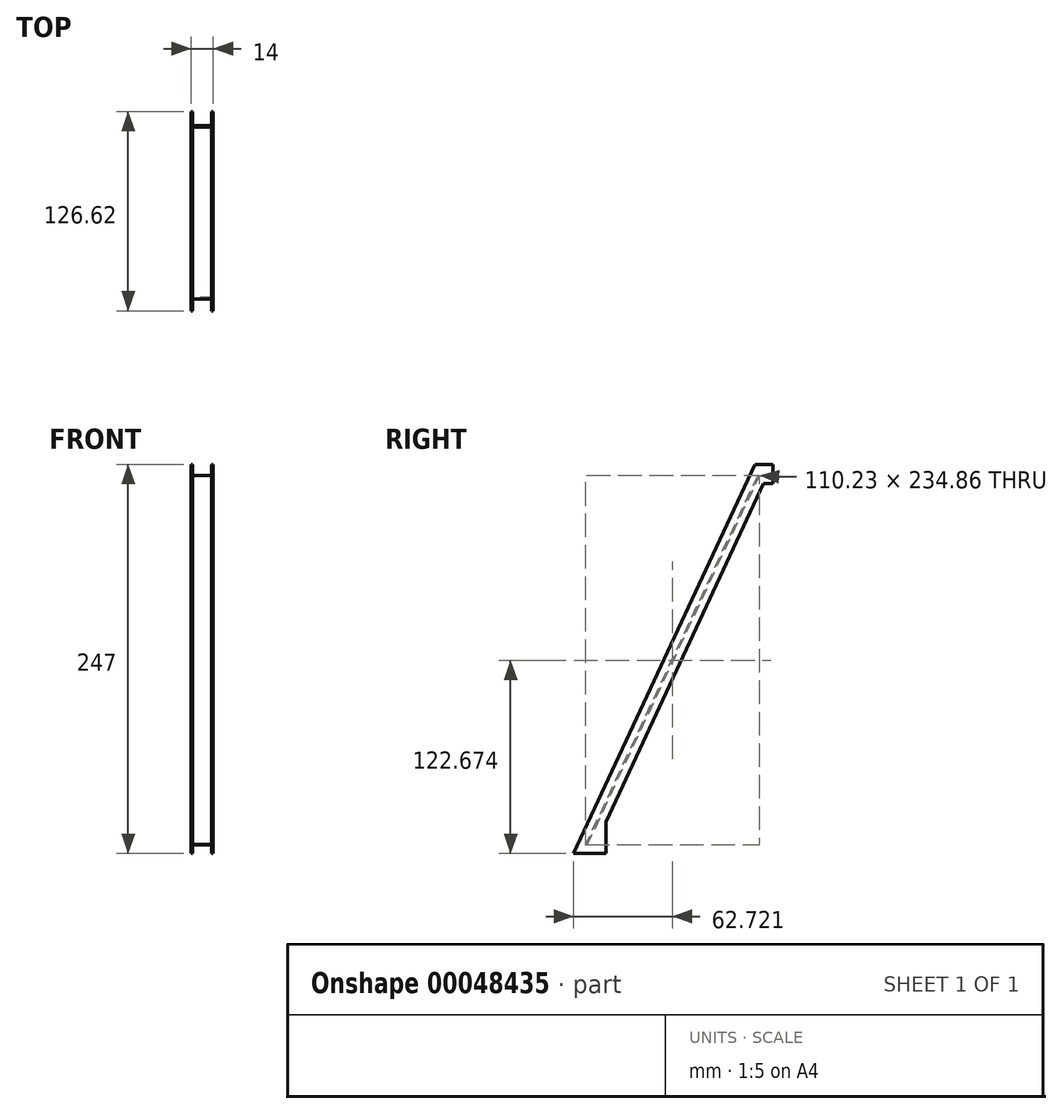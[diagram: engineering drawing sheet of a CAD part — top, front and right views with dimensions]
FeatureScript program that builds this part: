
annotation { "Feature Type Name" : "Feature", "Feature Type Description" : "" }
export const myFeature = defineFeature(function(context is Context, id is Id, definition is map)
    precondition{}
    {
        {
            var Q0;
            Q0=qCreatedBy(makeId("Right.planeOp"),FACE);
            cPlane(context, id + "F0", {"entities" : qUnion([Q0]), "cplaneType" : CPlaneType.OFFSET, "offset" : 7 * mm, "oppositeDirection" : true, "width" : 150 * mm, "height" : 150 * mm});
        }
        {
            var Q0;
            Q0=qCreatedBy(id+"F0.planeOp",FACE);
            var sketch = newSketch(context, id + "F1", { "sketchPlane" : qUnion([Q0])});
            skLineSegment(sketch, "E0", {"start": v(0, 0) * mm, "end": v(115.18, 247) * mm});
            skLineSegment(sketch, "E1", {"start": v(115.18, 247) * mm, "end": v(126.62, 247) * mm});
            skLineSegment(sketch, "E2", {"start": v(126.62, 247) * mm, "end": v(126.62, 235) * mm});
            skLineSegment(sketch, "E3", {"start": v(126.62, 235) * mm, "end": v(120.62, 235) * mm});
            skLineSegment(sketch, "E4", {"start": v(120.62, 235) * mm, "end": v(20.36, 20) * mm});
            skLineSegment(sketch, "E5", {"start": v(20.36, 20) * mm, "end": v(20.36, 0) * mm});
            skLineSegment(sketch, "E6", {"start": v(20.36, 0) * mm, "end": v(0, 0) * mm});
            skSolve(sketch);
        }
        {
            var Q0;
            Q0=makeQuery(id+"F1.imprint","IMPRINT",FACE,{"disambiguationData":[TD([[makeQuery(id+"F1.imprint","IMPRINT",EDGE,{"derivedFrom":sQuery(id+"F1.wireOp",EDGE,"E0")}),-1.0]])]});
            extrude(context, id + "F2", {"entities" : qUnion([Q0]), "depth" : 1 * mm});
        }
        {
            var Q0;
            Q0=makeQuery(id+"F2.opExtrude","SWEPT_BODY",BODY,{"disambiguationData":[OSD([sQuery(id+"F1.wireOp",EDGE,"E0"),sQuery(id+"F1.wireOp",EDGE,"E1"),sQuery(id+"F1.wireOp",EDGE,"E2"),sQuery(id+"F1.wireOp",EDGE,"E3"),sQuery(id+"F1.wireOp",EDGE,"E4"),sQuery(id+"F1.wireOp",EDGE,"E5"),sQuery(id+"F1.wireOp",EDGE,"E6")])]});
            var Q1;
            Q1=qCreatedBy(makeId("Right.planeOp"),FACE);
            mirror(context, id + "F3", {"entities" : qUnion([Q0]), "mirrorPlane" : qUnion([Q1])});
        }
        {
            var Q0;
            Q0=qCreatedBy(makeId("Right.planeOp"),FACE);
            var sketch = newSketch(context, id + "F4", { "sketchPlane" : qUnion([Q0])});
            skLineSegment(sketch, "E7", {"start": v(115.18, 247) * mm, "end": v(120.62, 235) * mm, "construction": true});
            skLineSegment(sketch, "E8", {"start": v(117.9, 241) * mm, "end": v(5.52, 0) * mm, "construction": true});
            skLineSegment(sketch, "E9", {"start": v(116.93, 240.1) * mm, "end": v(7.6, 5.67) * mm});
            skLineSegment(sketch, "E10", {"start": v(7.6, 5.67) * mm, "end": v(8.51, 5.24) * mm});
            skLineSegment(sketch, "E11", {"start": v(8.51, 5.24) * mm, "end": v(117.83, 239.68) * mm});
            skLineSegment(sketch, "E12", {"start": v(117.83, 239.68) * mm, "end": v(116.93, 240.1) * mm});
            skSolve(sketch);
        }
        {
            var Q0;
            Q0 = qSketchRegion(id + "F4", true);
            extrude(context, id + "F5", {"entities" : qUnion([Q0]), "operationType" : NewBodyOperationType.ADD, "depth" : 6 * mm, "hasSecondDirection" : true, "secondDirectionOppositeDirection" : true, "secondDirectionDepth" : 6 * mm});
        }
    });
